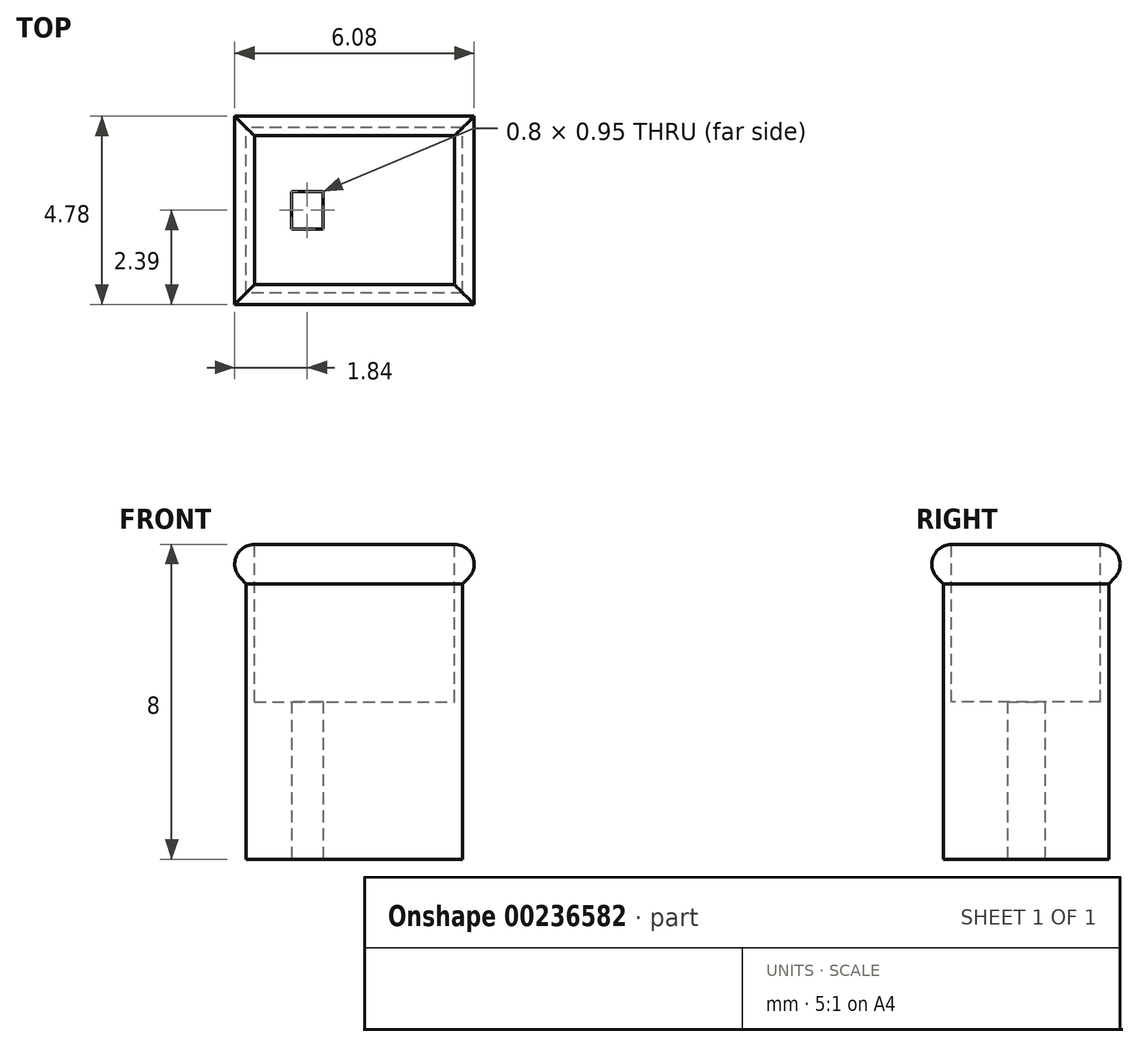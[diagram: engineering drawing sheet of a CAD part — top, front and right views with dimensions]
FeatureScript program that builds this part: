
annotation { "Feature Type Name" : "Feature", "Feature Type Description" : "" }
export const myFeature = defineFeature(function(context is Context, id is Id, definition is map)
    precondition{}
    {
        {
            var Q0;
            Q0=qCreatedBy(makeId("Top.planeOp"),FACE);
            var sketch = newSketch(context, id + "F0", { "sketchPlane" : qUnion([Q0])});
            skLineSegment(sketch, "E0.bottom", {"start": v(2.75, -2.1) * mm, "end": v(-2.75, -2.1) * mm});
            skLineSegment(sketch, "E0.top", {"start": v(2.75, 2.1) * mm, "end": v(-2.75, 2.1) * mm});
            skLineSegment(sketch, "E0.left", {"start": v(2.75, -2.1) * mm, "end": v(2.75, 2.1) * mm});
            skLineSegment(sketch, "E0.right", {"start": v(-2.75, -2.1) * mm, "end": v(-2.75, 2.1) * mm});
            skPoint(sketch, "E0.middle", {"position": v(0, 0) * mm});
            skSolve(sketch);
        }
        {
            var Q0;
            Q0 = qSketchRegion(id + "F0", true);
            extrude(context, id + "F1", {"entities" : qUnion([Q0]), "depth" : 7 * mm});
        }
        {
            var Q0;
            Q0=qCreatedBy(makeId("Top.planeOp"),FACE);
            var sketch = newSketch(context, id + "F2", { "sketchPlane" : qUnion([Q0])});
            skLineSegment(sketch, "E1.bottom", {"start": v(-0.8, -0.47) * mm, "end": v(-1.6, -0.47) * mm});
            skLineSegment(sketch, "E1.top", {"start": v(-0.8, 0.48) * mm, "end": v(-1.6, 0.47) * mm});
            skLineSegment(sketch, "E1.left", {"start": v(-0.8, -0.47) * mm, "end": v(-0.8, 0.48) * mm});
            skLineSegment(sketch, "E1.right", {"start": v(-1.6, -0.47) * mm, "end": v(-1.6, 0.47) * mm});
            skPoint(sketch, "E1.middle", {"position": v(-1.2, 0) * mm});
            skSolve(sketch);
        }
        {
            var Q0;
            Q0 = qSketchRegion(id + "F2", true);
            extrude(context, id + "F3", {"entities" : qUnion([Q0]), "operationType" : NewBodyOperationType.REMOVE, "depth" : 5 * mm});
        }
        {
            var Q0;
            Q0=makeQuery(id+"F1.opExtrude","CAP_FACE",FACE,{"disambiguationData":[OSD([sQuery(id+"F0.wireOp",EDGE,"E0.bottom"),sQuery(id+"F0.wireOp",EDGE,"E0.top"),sQuery(id+"F0.wireOp",EDGE,"E0.left"),sQuery(id+"F0.wireOp",EDGE,"E0.right")])],"isStart":false});
            extrude(context, id + "F4", {"entities" : qUnion([Q0]), "operationType" : NewBodyOperationType.ADD, "depth" : 1 * mm, "hasDraft" : true, "draftAngle" : 45 * degree});
        }
        {
            var Q0;
            Q0=qCreatedBy(makeId("Top.planeOp"),FACE);
            var sketch = newSketch(context, id + "F5", { "sketchPlane" : qUnion([Q0])});
            skLineSegment(sketch, "E2.0", {"start": v(-0.65, 0.63) * mm, "end": v(-0.65, -0.62) * mm});
            skLineSegment(sketch, "E2.1", {"start": v(-1.75, 0.62) * mm, "end": v(-0.65, 0.63) * mm});
            skLineSegment(sketch, "E2.2", {"start": v(-1.75, -0.62) * mm, "end": v(-1.75, 0.62) * mm});
            skLineSegment(sketch, "E2.3", {"start": v(-0.65, -0.62) * mm, "end": v(-1.75, -0.62) * mm});
            skSolve(sketch);
        }
        {
            var Q0;
            Q0=makeQuery(id+"F4.opExtrude","CAP_FACE",FACE,{"disambiguationData":[OSD([sQuery(id+"F0.wireOp",EDGE,"E0.bottom"),sQuery(id+"F0.wireOp",EDGE,"E0.top"),sQuery(id+"F0.wireOp",EDGE,"E0.left"),sQuery(id+"F0.wireOp",EDGE,"E0.right")])],"isStart":false});
            fillet(context, id + "F6", {"entities" : qUnion([Q0]), "radius" : 0.5 * mm, "tangentPropagation" : true, "allowEdgeOverflow" : false});
        }
        {
            var Q0;
            Q0=makeQuery(id+"F4.opExtrude","CAP_FACE",FACE,{"disambiguationData":[OSD([sQuery(id+"F0.wireOp",EDGE,"E0.bottom"),sQuery(id+"F0.wireOp",EDGE,"E0.top"),sQuery(id+"F0.wireOp",EDGE,"E0.left"),sQuery(id+"F0.wireOp",EDGE,"E0.right")])],"isStart":false});
            extrude(context, id + "F8", {"entities" : qUnion([Q0]), "operationType" : NewBodyOperationType.REMOVE, "oppositeDirection" : true, "depth" : 4 * mm});
        }
    });
